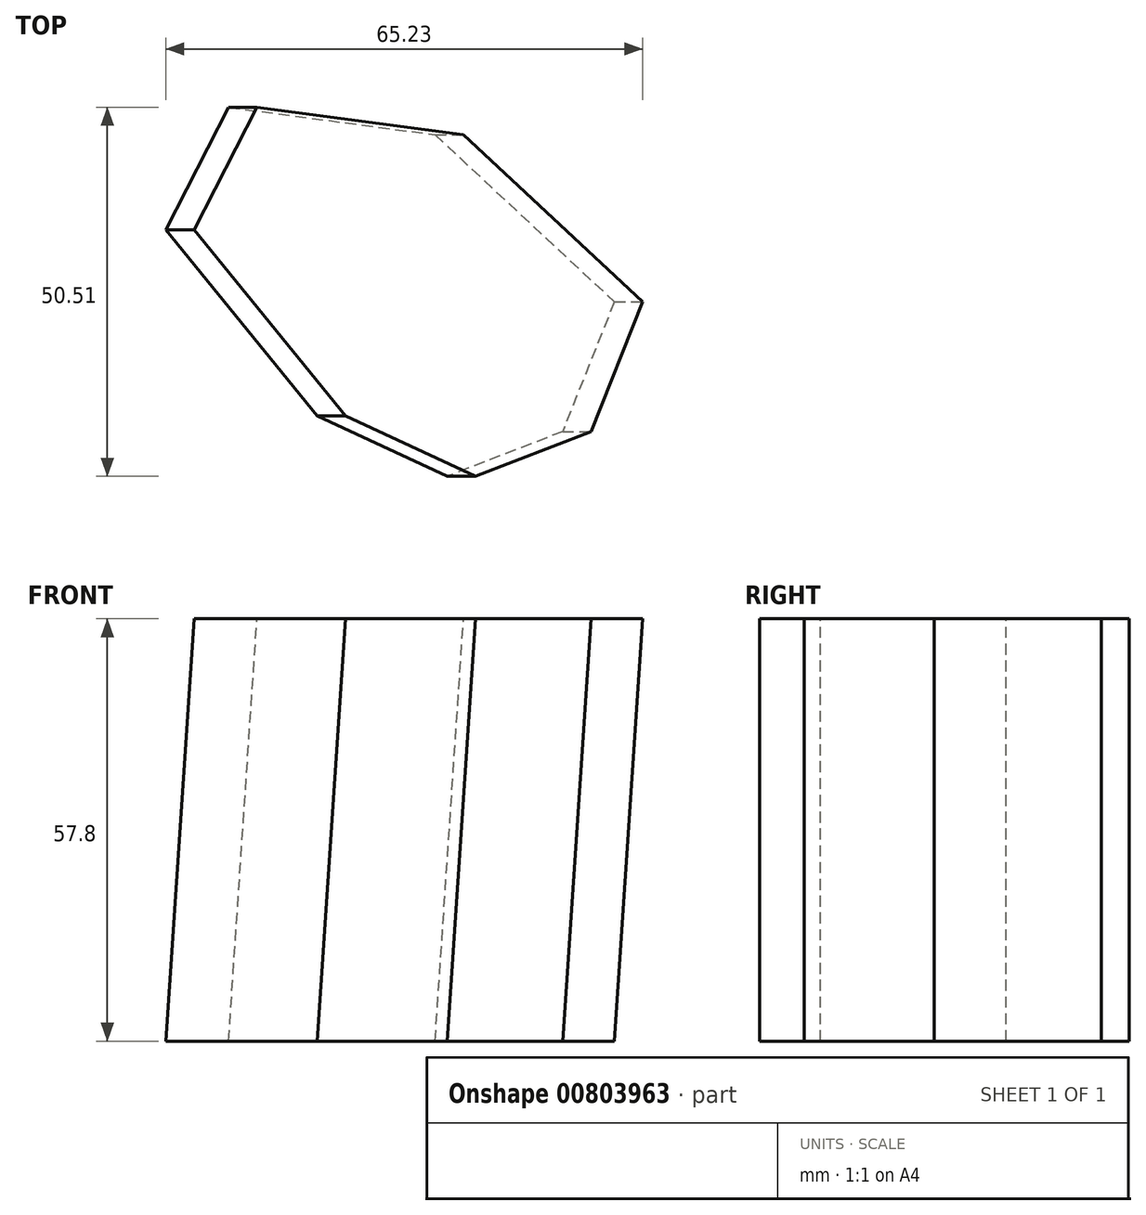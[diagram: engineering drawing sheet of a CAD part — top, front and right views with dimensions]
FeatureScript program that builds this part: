
annotation { "Feature Type Name" : "Feature", "Feature Type Description" : "" }
export const myFeature = defineFeature(function(context is Context, id is Id, definition is map)
    precondition{}
    {
        {
            var Q0;
            Q0=qCreatedBy(makeId("Top.planeOp"),FACE);
            var sketch = newSketch(context, id + "F0", { "sketchPlane" : qUnion([Q0])});
            skLineSegment(sketch, "E0", {"start": v(-10.73, -15.57) * mm, "end": v(-31.44, 9.87) * mm});
            skLineSegment(sketch, "E1", {"start": v(-31.44, 9.87) * mm, "end": v(-22.85, 26.64) * mm});
            skLineSegment(sketch, "E2", {"start": v(-22.85, 26.64) * mm, "end": v(5.4, 22.88) * mm});
            skLineSegment(sketch, "E3", {"start": v(5.4, 22.88) * mm, "end": v(29.9, 0) * mm});
            skLineSegment(sketch, "E4", {"start": v(29.9, 0) * mm, "end": v(22.83, -17.75) * mm});
            skLineSegment(sketch, "E5", {"start": v(22.83, -17.75) * mm, "end": v(7.03, -23.87) * mm});
            skLineSegment(sketch, "E6", {"start": v(7.03, -23.87) * mm, "end": v(-10.73, -15.57) * mm});
            skSolve(sketch);
        }
        {
            var Q0;
            Q0=qCreatedBy(makeId("Front.planeOp"),FACE);
            var sketch = newSketch(context, id + "F1", { "sketchPlane" : qUnion([Q0])});
            skLineSegment(sketch, "E7", {"start": v(0, 0) * mm, "end": v(3.88, 57.8) * mm});
            skSolve(sketch);
        }
        {
            var Q0;
            Q0=makeQuery(id+"F0.imprint","IMPRINT",FACE,{"disambiguationData":[TD([[makeQuery(id+"F0.imprint","IMPRINT",EDGE,{"derivedFrom":sQuery(id+"F0.wireOp",EDGE,"E0")}),-1.0]])]});
            var Q1;
            Q1=sQuery(id+"F1.wireOp",EDGE,"E7");
            sweep(context, id + "F2", {"profiles" : qUnion([Q0]), "path" : qUnion([Q1])});
        }
    });
